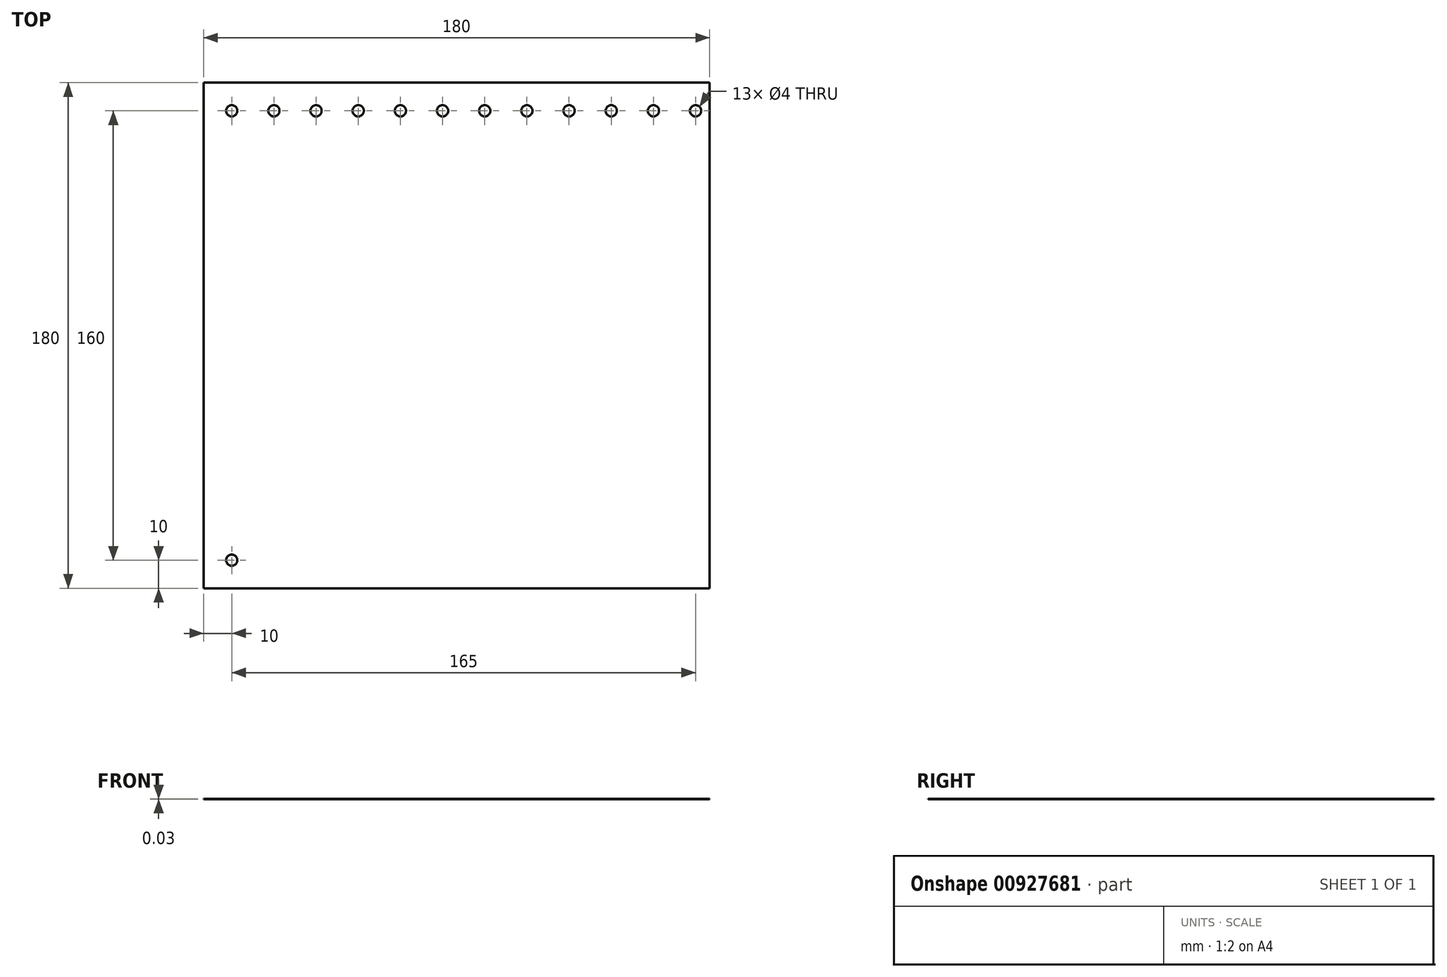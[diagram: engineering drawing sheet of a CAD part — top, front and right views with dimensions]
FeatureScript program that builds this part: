
annotation { "Feature Type Name" : "Feature", "Feature Type Description" : "" }
export const myFeature = defineFeature(function(context is Context, id is Id, definition is map)
    precondition{}
    {
        {
            var Q0;
            Q0=qCreatedBy(makeId("Top.planeOp"),FACE);
            var sketch = newSketch(context, id + "F0", { "sketchPlane" : qUnion([Q0])});
            skLineSegment(sketch, "E0.bottom", {"start": v(90, -90) * mm, "end": v(-90, -90) * mm});
            skLineSegment(sketch, "E0.top", {"start": v(90, 90) * mm, "end": v(-90, 90) * mm});
            skLineSegment(sketch, "E0.left", {"start": v(90, -90) * mm, "end": v(90, 90) * mm});
            skLineSegment(sketch, "E0.right", {"start": v(-90, -90) * mm, "end": v(-90, 90) * mm});
            skPoint(sketch, "E0.middle", {"position": v(0, 0) * mm});
            skSolve(sketch);
        }
        {
            var Q0;
            Q0=makeQuery(id+"F0.imprint","IMPRINT",FACE,{"disambiguationData":[TD([[makeQuery(id+"F0.imprint","IMPRINT",EDGE,{"derivedFrom":sQuery(id+"F0.wireOp",EDGE,"E0.bottom")}),-1.0]])]});
            extrude(context, id + "F1", {"entities" : qUnion([Q0]), "depth" : 0.03 * mm, "offsetDistance" : 25 * mm});
        }
        {
            var Q0;
            Q0=makeQuery(id+"F1.opExtrude","CAP_FACE",FACE,{"disambiguationData":[OSD([sQuery(id+"F0.wireOp",EDGE,"E0.bottom"),sQuery(id+"F0.wireOp",EDGE,"E0.top"),sQuery(id+"F0.wireOp",EDGE,"E0.left"),sQuery(id+"F0.wireOp",EDGE,"E0.right")])],"isStart":false});
            var sketch = newSketch(context, id + "F2", { "sketchPlane" : qUnion([Q0])});
            skCircle(sketch, "E1", {"center": v(-80, -80) * mm, "radius": 2 * mm});
            skCircle(sketch, "E2.1.0.0", {"center": v(-65, -80) * mm, "radius": 2 * mm});
            skCircle(sketch, "E2.2.0.0", {"center": v(-50, -80) * mm, "radius": 2 * mm});
            skCircle(sketch, "E2.3.0.0", {"center": v(-35, -80) * mm, "radius": 2 * mm});
            skCircle(sketch, "E2.4.0.0", {"center": v(-20, -80) * mm, "radius": 2 * mm});
            skCircle(sketch, "E2.5.0.0", {"center": v(-5, -80) * mm, "radius": 2 * mm});
            skCircle(sketch, "E2.6.0.0", {"center": v(10, -80) * mm, "radius": 2 * mm});
            skCircle(sketch, "E2.7.0.0", {"center": v(25, -80) * mm, "radius": 2 * mm});
            skCircle(sketch, "E2.8.0.0", {"center": v(40, -80) * mm, "radius": 2 * mm});
            skCircle(sketch, "E2.9.0.0", {"center": v(55, -80) * mm, "radius": 2 * mm});
            skCircle(sketch, "E2.10.0.0", {"center": v(70, -80) * mm, "radius": 2 * mm});
            skLineSegment(sketch, "E2.direction1", {"start": v(-80, -80) * mm, "end": v(-65, -80) * mm, "construction": true});
            skSolve(sketch);
        }
        {
            var Q0;
            Q0=sQuery(id+"F2.wireOp",VERTEX,"E1.center");
            var Q1;
            Q1=makeQuery(id+"F1.opExtrude","SWEPT_BODY",BODY,{"disambiguationData":[OSD([sQuery(id+"F0.wireOp",EDGE,"E0.bottom"),sQuery(id+"F0.wireOp",EDGE,"E0.top"),sQuery(id+"F0.wireOp",EDGE,"E0.left"),sQuery(id+"F0.wireOp",EDGE,"E0.right")])]});
            hole(context, id + "F3", {"style" : HoleStyle.SIMPLE, "endStyle" : HoleEndStyle.THROUGH, "holeDiameter" : 4 * mm, "majorDiameter" : 5 * mm, "isTappedThrough" : true, "tappedDepth" : 12 * mm, "tapClearance" : 3, "locations" : qUnion([Q0]), "scope" : qUnion([Q1])});
        }
        {
            var Q0;
            Q0=makeQuery(id+"F1.opExtrude","CAP_FACE",FACE,{"disambiguationData":[OSD([sQuery(id+"F0.wireOp",EDGE,"E0.bottom"),sQuery(id+"F0.wireOp",EDGE,"E0.top"),sQuery(id+"F0.wireOp",EDGE,"E0.left"),sQuery(id+"F0.wireOp",EDGE,"E0.right")])],"isStart":false});
            var sketch = newSketch(context, id + "F4", { "sketchPlane" : qUnion([Q0])});
            skCircle(sketch, "E3", {"center": v(-80, 80) * mm, "radius": 2 * mm});
            skCircle(sketch, "E4.1.0.0", {"center": v(-65, 80) * mm, "radius": 2 * mm});
            skCircle(sketch, "E4.2.0.0", {"center": v(-50, 80) * mm, "radius": 2 * mm});
            skCircle(sketch, "E4.3.0.0", {"center": v(-35, 80) * mm, "radius": 2 * mm});
            skCircle(sketch, "E4.4.0.0", {"center": v(-20, 80) * mm, "radius": 2 * mm});
            skCircle(sketch, "E4.5.0.0", {"center": v(-5, 80) * mm, "radius": 2 * mm});
            skCircle(sketch, "E4.6.0.0", {"center": v(10, 80) * mm, "radius": 2 * mm});
            skCircle(sketch, "E4.7.0.0", {"center": v(25, 80) * mm, "radius": 2 * mm});
            skCircle(sketch, "E4.8.0.0", {"center": v(40, 80) * mm, "radius": 2 * mm});
            skCircle(sketch, "E4.9.0.0", {"center": v(55, 80) * mm, "radius": 2 * mm});
            skCircle(sketch, "E4.10.0.0", {"center": v(70, 80) * mm, "radius": 2 * mm});
            skCircle(sketch, "E4.11.0.0", {"center": v(85, 80) * mm, "radius": 2 * mm});
            skLineSegment(sketch, "E4.direction1", {"start": v(-80, 80) * mm, "end": v(-65, 80) * mm, "construction": true});
            skSolve(sketch);
        }
        {
            var Q0;
            Q0 = qSketchRegion(id + "F4", true);
            extrude(context, id + "F5", {"entities" : qUnion([Q0]), "operationType" : NewBodyOperationType.REMOVE, "endBound" : BoundingType.UP_TO_NEXT, "oppositeDirection" : true, "depth" : 25 * mm, "offsetDistance" : 25 * mm});
        }
    });
